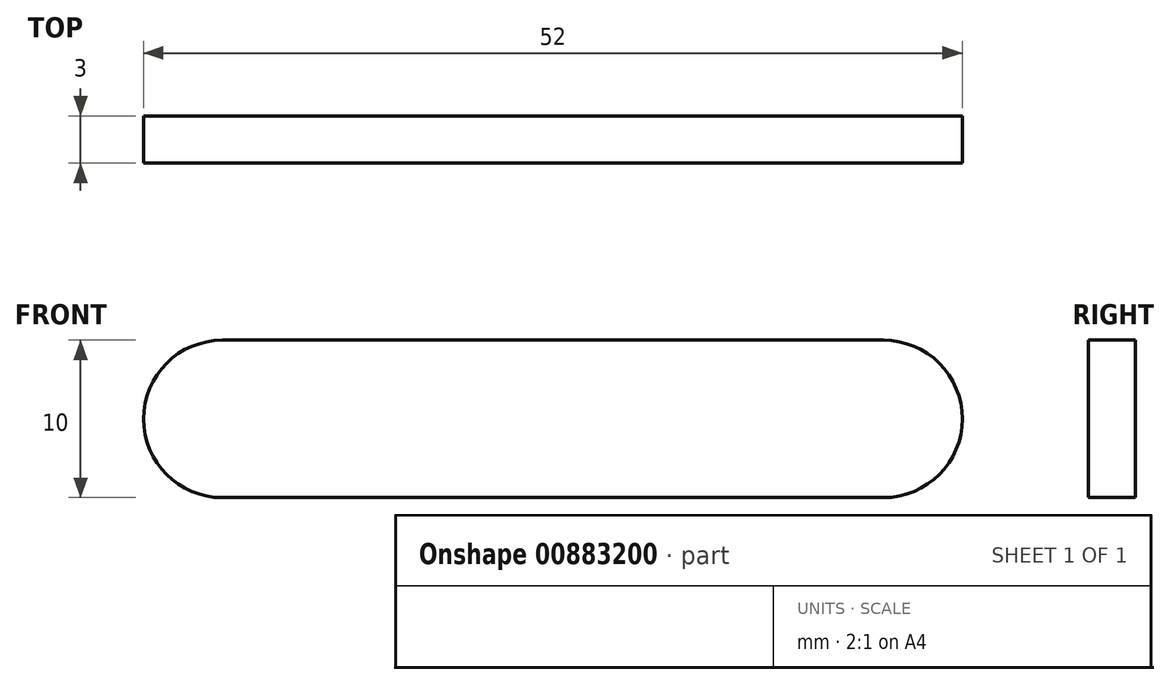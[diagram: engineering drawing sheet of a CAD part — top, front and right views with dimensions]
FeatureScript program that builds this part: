
annotation { "Feature Type Name" : "Feature", "Feature Type Description" : "" }
export const myFeature = defineFeature(function(context is Context, id is Id, definition is map)
    precondition{}
    {
        {
            var Q0;
            Q0=qCreatedBy(makeId("Front.planeOp"),FACE);
            var sketch = newSketch(context, id + "F0", { "sketchPlane" : qUnion([Q0])});
            skLineSegment(sketch, "E0.bottom", {"start": v(0, 0) * mm, "end": v(42, 0) * mm});
            skLineSegment(sketch, "E0.top", {"start": v(0, 10) * mm, "end": v(42, 10) * mm});
            skLineSegment(sketch, "E0.left", {"start": v(0, 0) * mm, "end": v(0, 10) * mm});
            skLineSegment(sketch, "E0.right", {"start": v(42, 0) * mm, "end": v(42, 10) * mm});
            skArc(sketch, "E1", {"start": v(0, 10) * mm, "mid": v(-5, 5) * mm, "end": v(0, 0) * mm});
            skArc(sketch, "E2", {"start": v(42, 0) * mm, "mid": v(47, 5) * mm, "end": v(42, 10) * mm});
            skSolve(sketch);
        }
        {
            var Q0;
            Q0 = qSketchRegion(id + "F0", true);
            extrude(context, id + "F1", {"entities" : qUnion([Q0]), "depth" : 3 * mm, "offsetDistance" : 25 * mm});
        }
    });
